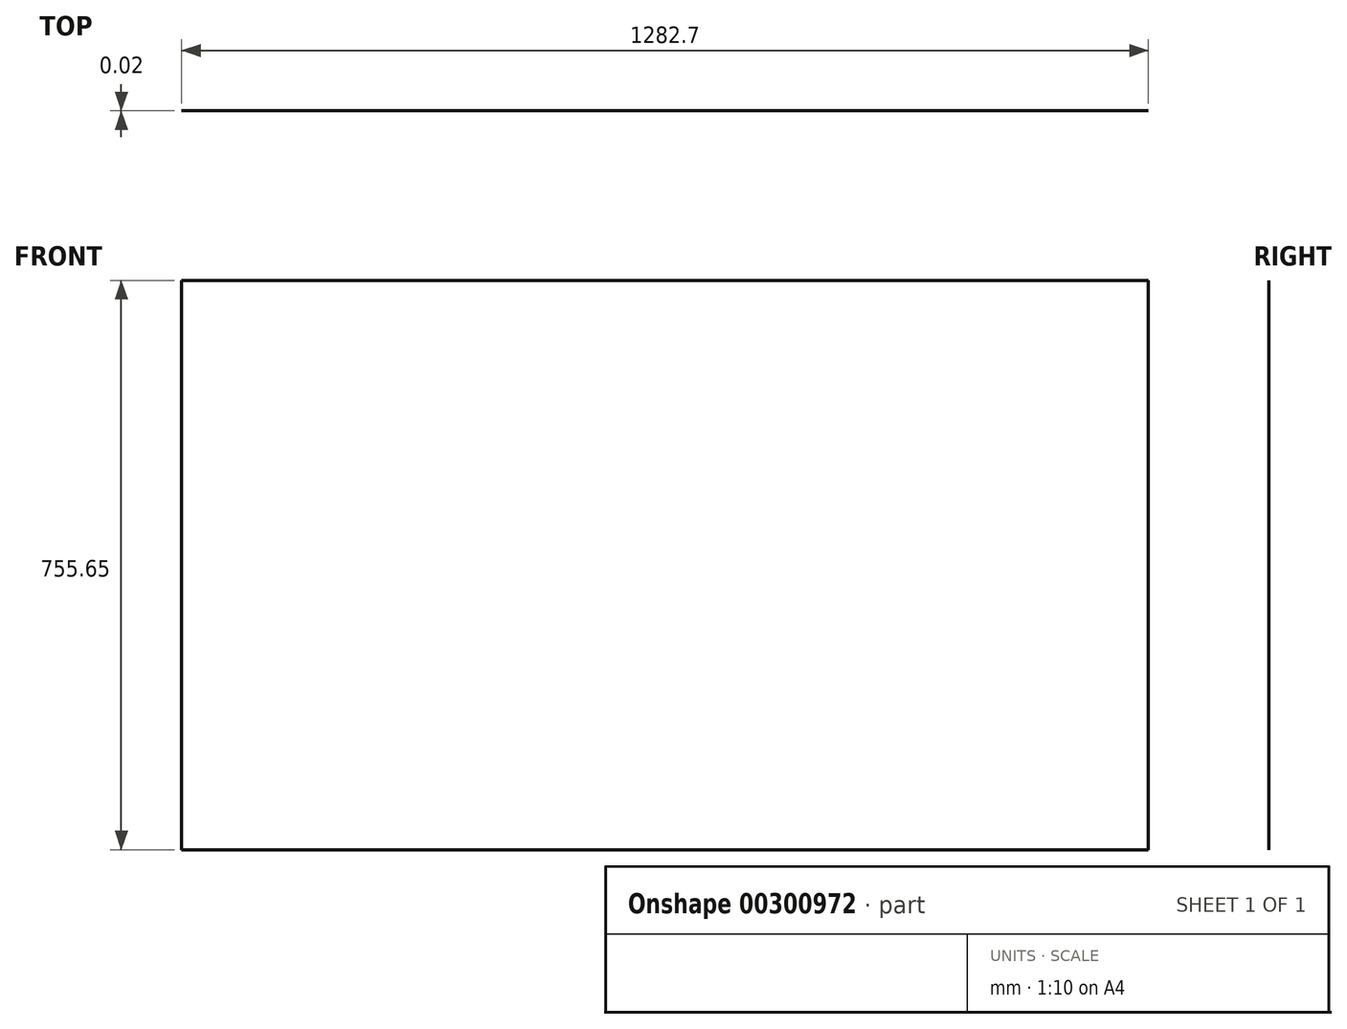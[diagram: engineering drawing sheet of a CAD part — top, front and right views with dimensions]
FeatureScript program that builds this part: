
annotation { "Feature Type Name" : "Feature", "Feature Type Description" : "" }
export const myFeature = defineFeature(function(context is Context, id is Id, definition is map)
    precondition{}
    {
        {
            var Q0;
            Q0=qCreatedBy(makeId("Front.planeOp"),FACE);
            var sketch = newSketch(context, id + "F0", { "sketchPlane" : qUnion([Q0])});
            skLineSegment(sketch, "E0.bottom", {"start": v(0, 0) * mm, "end": v(1282.7, 0) * mm});
            skLineSegment(sketch, "E0.top", {"start": v(0, 755.65) * mm, "end": v(1282.7, 755.65) * mm});
            skLineSegment(sketch, "E0.left", {"start": v(0, 0) * mm, "end": v(0, 755.65) * mm});
            skLineSegment(sketch, "E0.right", {"start": v(1282.7, 0) * mm, "end": v(1282.7, 755.65) * mm});
            skSolve(sketch);
        }
        {
            var Q0;
            Q0=qSketchRegion(id+"F0",true);
            extrude(context, id + "F1", {"entities" : qUnion([Q0]), "depth" : 5 / 203.2 * mm});
        }
    });
